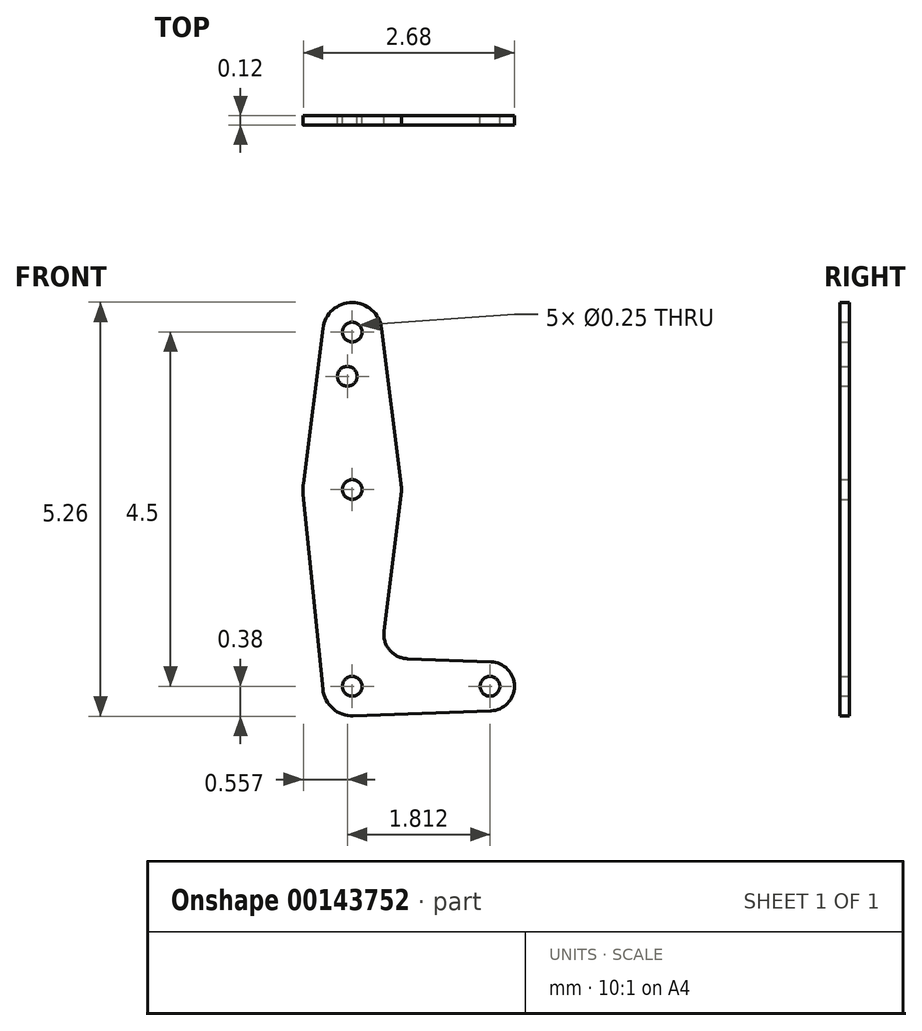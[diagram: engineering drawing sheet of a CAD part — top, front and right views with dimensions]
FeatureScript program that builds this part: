
annotation { "Feature Type Name" : "Feature", "Feature Type Description" : "" }
export const myFeature = defineFeature(function(context is Context, id is Id, definition is map)
    precondition{}
    {
        {
            var Q0;
            Q0=qCreatedBy(makeId("Front.planeOp"),FACE);
            var sketch = newSketch(context, id + "F0", { "sketchPlane" : qUnion([Q0])});
            skCircle(sketch, "E0", {"center": v(0, 0) * mm, "radius": 0.38 * mm});
            skCircle(sketch, "E1", {"center": v(0, 4.5) * mm, "radius": 0.38 * mm});
            skLineSegment(sketch, "E2", {"start": v(0, 0) * mm, "end": v(0, 4.5) * mm, "construction": true});
            skCircle(sketch, "E3", {"center": v(0, 2.5) * mm, "radius": 0.62 * mm});
            skCircle(sketch, "E4", {"center": v(1.75, 0) * mm, "radius": 0.31 * mm});
            skLineSegment(sketch, "E5", {"start": v(0, 0) * mm, "end": v(1.75, 0) * mm, "construction": true});
            skLineSegment(sketch, "E6", {"start": v(-0.37, 4.55) * mm, "end": v(-0.62, 2.58) * mm});
            skLineSegment(sketch, "E7", {"start": v(0.37, 4.55) * mm, "end": v(0.62, 2.58) * mm});
            skLineSegment(sketch, "E8", {"start": v(0.7, 0.35) * mm, "end": v(1.76, 0.31) * mm});
            skLineSegment(sketch, "E9", {"start": v(0, -0.38) * mm, "end": v(1.76, -0.31) * mm});
            skLineSegment(sketch, "E10", {"start": v(0.62, 2.42) * mm, "end": v(0.4, 0.7) * mm});
            skCircle(sketch, "E11", {"center": v(-0.06, 3.94) * mm, "radius": 0.12 * mm});
            skCircle(sketch, "E12", {"center": v(0, 4.5) * mm, "radius": 0.12 * mm});
            skCircle(sketch, "E13", {"center": v(0, 2.5) * mm, "radius": 0.12 * mm});
            skCircle(sketch, "E14", {"center": v(0, 0) * mm, "radius": 0.12 * mm});
            skCircle(sketch, "E15", {"center": v(1.75, 0) * mm, "radius": 0.12 * mm});
            skArc(sketch, "E16.filletArc", {"start": v(0.4, 0.7) * mm, "mid": v(0.48, 0.46) * mm, "end": v(0.7, 0.35) * mm});
            skLineSegment(sketch, "E17", {"start": v(-0.62, 2.44) * mm, "end": v(-0.37, -0.04) * mm});
            skSolve(sketch);
        }
        {
            var Q0;
            Q0=qSketchRegion(id+"F0",true);
            extrude(context, id + "F1", {"entities" : qUnion([Q0]), "depth" : 0.12 * mm});
        }
    });
